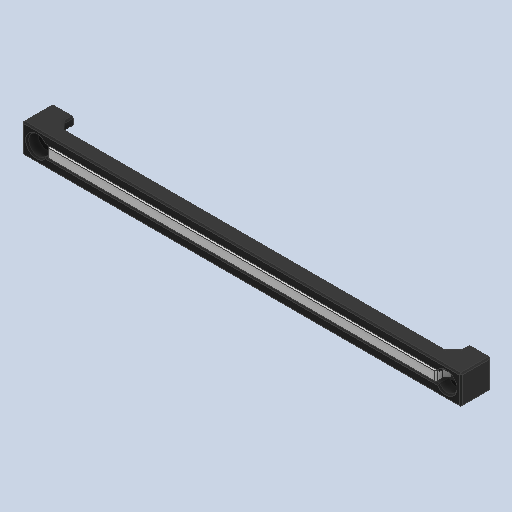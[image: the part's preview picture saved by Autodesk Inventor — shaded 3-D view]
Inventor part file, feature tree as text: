
AUTODESK INVENTOR PART (.ipt)
format: ipt  version: 2024.2 (Build 282272000, 272)  size: 804,352 bytes
history: native  units: mm
features: extrude x14, chamfer x10, thicken_offset x5, fillet x4, plane x3, mirror x3, projected_geometry x3, sketch x2
ambient origin geometry x8: Origin, YZ Plane, XZ Plane, XY Plane, X Axis, Y Axis, Z Axis, Center Point
bodies: Solid1 (feature_tree), Solid2 (feature_tree)
feature tree (44):
  extrude  "Extrusion1"  Depth=10.0mm
  extrude  "Extrusion2"  Depth=1.5mm
  extrude  "Extrusion3"  Depth=1.5mm
  plane  "Work Plane1"
  extrude  "Extrusion5"  Depth=5.0mm
  extrude  "Extrusion6"  TaperAngle=0.0deg  [1 undecoded]
  plane  "Work Plane2"
  extrude  "Extrusion7"  Depth=1.5mm
  mirror  "Mirror1"
  chamfer  "Chamfer3"  Distance=2.0mm
  chamfer  "Chamfer5"  Distance=5.6mm
  chamfer  "Chamfer6"  Distance=2.0mm
  extrude  "Extrusion8"  Depth=1.5mm
  chamfer  "Chamfer7"  [1 undecoded]
  chamfer  "Chamfer8"  [1 undecoded]
  thicken_offset  "Thicken1"
  thicken_offset  "Thicken2"
  chamfer  "Chamfer9"  Distance=3.75mm
  extrude  "Extrusion9"  Depth=1.5mm
  chamfer  "Chamfer11"  Distance=3.0mm
  extrude  "Extrusion10"  Depth=1.5mm
  extrude  "Extrusion11"  Depth=1.5mm
  mirror  "Mirror2"
  extrude  "Extrusion12"  Depth=1.5mm TaperAngle=45.0deg
  mirror  "Mirror3"
  extrude  "Extrusion13"  Depth=1.5mm TaperAngle=45.0deg
  extrude  "Extrusion14"  Depth=1.5mm
  fillet  "Fillet2"  Radius=1.9mm
  chamfer  "Chamfer14"  [1 undecoded]
  chamfer  "Chamfer15"  Distance=0.5mm Angle=45.0deg
  fillet  "Fillet4"  Radius=0.5mm
  thicken_offset  "Thicken3"
  fillet  "Fillet5"  Radius=0.2mm
  thicken_offset  "Thicken4"
  thicken_offset  "Thicken5"
  fillet  "Fillet6"  Radius=0.2mm
  extrude  "Extrusion15"  Depth=1.5mm
  chamfer  "Chamfer16"  Distance=0.2mm
  sketch  "Sketch3"  dims[d0=150.0mm d1=10.0mm]
  projected_geometry  "Projected Loop1"
  plane  "Work Plane3"
  projected_geometry  "Projected Loop2"
  projected_geometry  "Projected Loop3"
  sketch  "Sketch12"  dims[d2=10.0mm d3=0.0mm d7=67.5mm d8=135.0mm d9=5.0mm d10=0.0mm d11=0.0mm d12=1.6mm d13=2.0mm d14=0.0mm d18=5.6mm d21=2.0mm d22=3.75mm d23=0.0mm d25=5.3mm d27=0.0mm d28=0.0mm d29=-2.0mm d30=3.75mm d31=0.0mm d32=2.0mm d33=3.0mm d34=2.8mm d35=5.6mm d39=0.5mm d40=2.0mm d41=45.0deg d45=0.5mm d46=2.0mm d47=45.0deg d48=70.0mm d49=1.9mm d50=2.0mm d51=45.0deg d52=0.0mm d53=0.0mm d54=0.5mm d55=2.0mm d56=45.0deg d57=0.5mm d58=2.0mm d59=45.0deg d60=0.2mm d61=0.2mm d62=0.2mm d63=0.2mm d64=0.5mm d65=2.0mm d66=45.0deg d70=6.5mm d71=3.0mm d72=5.0mm d73=2.5mm d74=0.0mm d75=0.5mm d76=2.0mm d77=45.0deg d78=0.0mm d79=0.0mm d80=10.0mm d81=0.0mm d88=3.0mm d89=0.0mm d90=0.0mm d91=0.0mm d93=0.56mm d94=3.0mm d95=0.0mm d96=1.5mm d97=0.5mm d98=2.0mm d99=45.0deg d101=0.5mm d102=2.0mm d103=45.0deg d104=1.5mm d105=0.25mm d106=0.25mm d107=0.5mm d108=2.116859mm d109=0.25mm d110=0.25mm d111=0.25mm d112=0.25mm d113=1.5mm d114=3.1mm d115=0.35mm d116=1.55mm d117=3.0mm d118=0.0mm d119=0.5mm d120=2.0mm d121=45.0deg]
note: 4 required parameter values undecoded (feature->parameter linkage not recoverable at this tier; creation-order binding heuristic only, values carry confidence <= 0.55)
